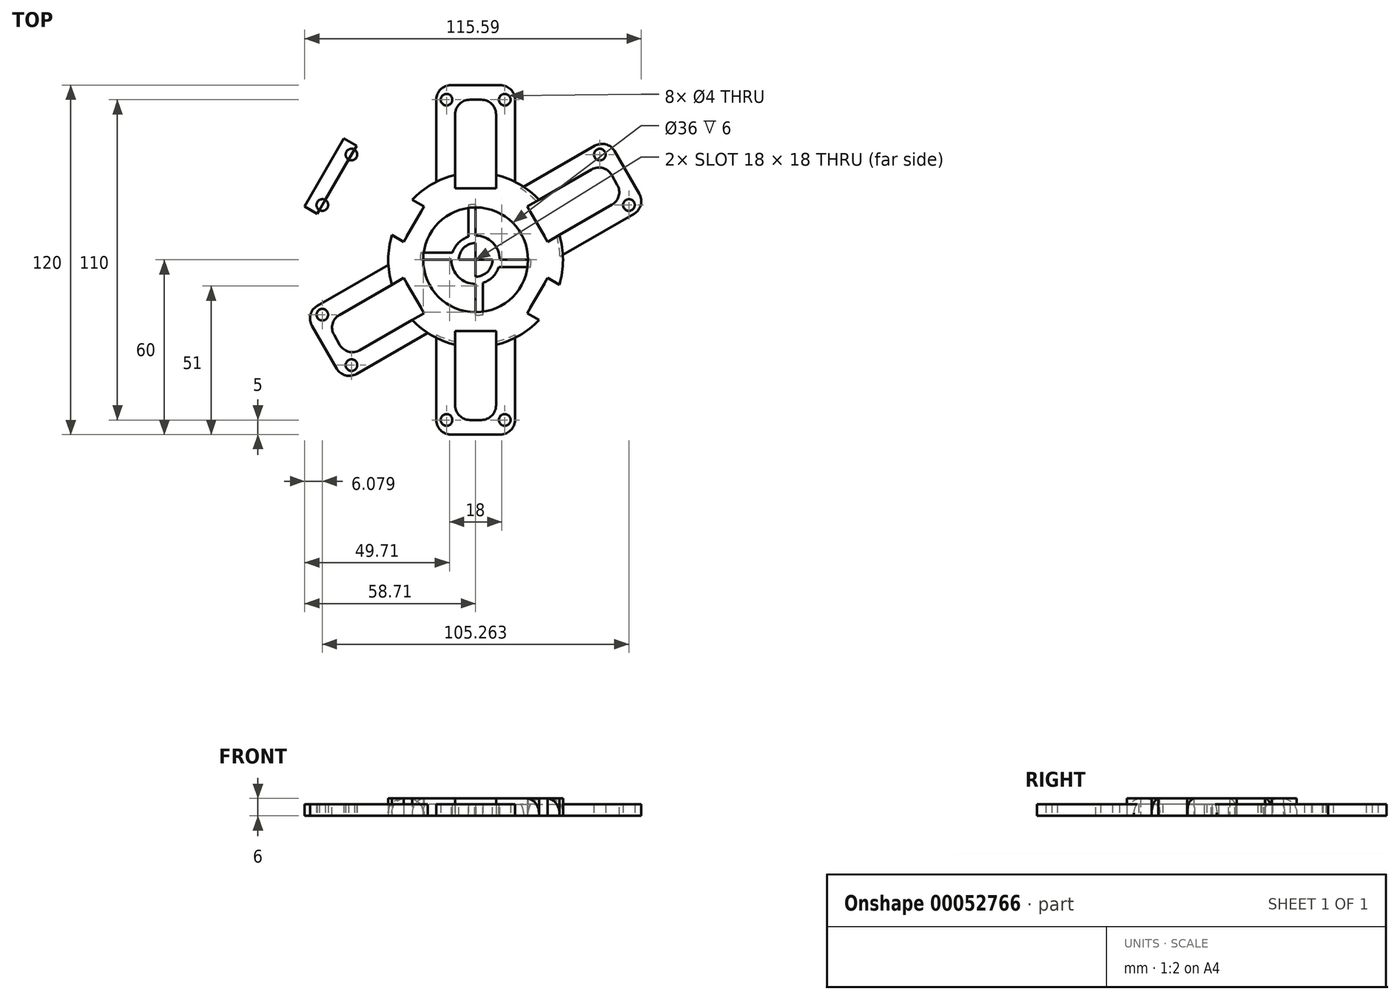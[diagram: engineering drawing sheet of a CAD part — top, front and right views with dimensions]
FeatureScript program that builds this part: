
annotation { "Feature Type Name" : "Feature", "Feature Type Description" : "" }
export const myFeature = defineFeature(function(context is Context, id is Id, definition is map)
    precondition{}
    {
        {
            assignVariable(context, id + "F0", {"name" : "RingH", "anyValue" : 6});
        }
        {
            assignVariable(context, id + "F1", {"name" : "CenterH", "anyValue" : 4});
        }
        {
            var Q0;
            Q0=qCreatedBy(makeId("Top.planeOp"),FACE);
            var sketch = newSketch(context, id + "F2", { "sketchPlane" : qUnion([Q0])});
            skCircle(sketch, "E0", {"center": v(0, 0) * mm, "radius": 18 * mm});
            skArc(sketch, "E1", {"start": v(7, -29.17) * mm, "mid": v(0, 30) * mm, "end": v(-7, -29.17) * mm});
            skLineSegment(sketch, "E2.top", {"start": v(-13.5, -60) * mm, "end": v(13.5, -60) * mm});
            skLineSegment(sketch, "E3", {"start": v(-13.5, -26.8) * mm, "end": v(-13.5, -60) * mm});
            skLineSegment(sketch, "E4", {"start": v(13.5, -26.8) * mm, "end": v(13.5, -60) * mm});
            skLineSegment(sketch, "E5.1.0", {"start": v(58.71, 18.3) * mm, "end": v(45.21, 41.7) * mm});
            skLineSegment(sketch, "E5.1.1", {"start": v(16.45, 25.09) * mm, "end": v(45.21, 41.7) * mm});
            skLineSegment(sketch, "E5.1.2", {"start": v(29.95, 1.7) * mm, "end": v(58.71, 18.3) * mm});
            skLineSegment(sketch, "E5.2.0", {"start": v(-45.21, 41.7) * mm, "end": v(-58.71, 18.3) * mm});
            skLineSegment(sketch, "E5.2.1", {"start": v(-29.95, 1.7) * mm, "end": v(-58.71, 18.3) * mm});
            skLineSegment(sketch, "E5.2.2", {"start": v(-16.45, 25.09) * mm, "end": v(-45.21, 41.7) * mm});
            skLineSegment(sketch, "E6.0", {"start": v(-40.13, 40.5) * mm, "end": v(-55.13, 14.5) * mm});
            skLineSegment(sketch, "E7.0", {"start": v(52.63, 18.84) * mm, "end": v(51.63, 20.57) * mm});
            skPoint(sketch, "E8", {"position": v(-47.63, 27.5) * mm});
            skPoint(sketch, "E9", {"position": v(-42.63, 36.16) * mm});
            skPoint(sketch, "E10", {"position": v(-52.63, 18.84) * mm});
            skCircle(sketch, "E11", {"center": v(-42.63, 36.16) * mm, "radius": 2 * mm});
            skCircle(sketch, "E12", {"center": v(-52.63, 18.84) * mm, "radius": 2 * mm});
            skPoint(sketch, "E13", {"position": v(47.63, 27.5) * mm});
            skPoint(sketch, "E14", {"position": v(42.63, 36.16) * mm});
            skPoint(sketch, "E15", {"position": v(52.63, 18.84) * mm});
            skCircle(sketch, "E16", {"center": v(42.63, 36.16) * mm, "radius": 2 * mm});
            skCircle(sketch, "E17", {"center": v(52.63, 18.84) * mm, "radius": 2 * mm});
            skPoint(sketch, "E18.orphan", {"position": v(40.13, 40.5) * mm});
            skLineSegment(sketch, "E19.trimOffspring", {"start": v(43.63, 34.43) * mm, "end": v(42.63, 36.16) * mm});
            skPoint(sketch, "E20.orphan", {"position": v(55.13, 14.5) * mm});
            skPoint(sketch, "E21", {"position": v(0, -53.3) * mm});
            skPoint(sketch, "E22", {"position": v(-10, -55) * mm});
            skPoint(sketch, "E23", {"position": v(10, -55) * mm});
            skCircle(sketch, "E24", {"center": v(10, -55) * mm, "radius": 2 * mm});
            skCircle(sketch, "E25", {"center": v(-10, -55) * mm, "radius": 2 * mm});
            skLineSegment(sketch, "E26.trimOffspring", {"start": v(8.95, -53.3) * mm, "end": v(11.05, -53.3) * mm});
            skLineSegment(sketch, "E27.trimOffspring", {"start": v(-10.56, -55) * mm, "end": v(-10, -55) * mm});
            skPoint(sketch, "E28.0.start.orphan", {"position": v(-15, -53.3) * mm});
            skPoint(sketch, "E29.orphan", {"position": v(15, -53.3) * mm});
            skLineSegment(sketch, "E30", {"start": v(0, -24.51) * mm, "end": v(0, -53.3) * mm, "construction": true});
            skLineSegment(sketch, "E31.0", {"start": v(-7, -24.51) * mm, "end": v(-7, -55) * mm});
            skLineSegment(sketch, "E32.0", {"start": v(7, -24.51) * mm, "end": v(7, -55) * mm});
            skLineSegment(sketch, "E33", {"start": v(-7, -24.51) * mm, "end": v(7, -24.51) * mm});
            skLineSegment(sketch, "E34", {"start": v(-7, -55) * mm, "end": v(7, -55) * mm});
            skLineSegment(sketch, "E35.1.0", {"start": v(17.73, 18.32) * mm, "end": v(44.13, 33.56) * mm});
            skLineSegment(sketch, "E35.1.1", {"start": v(24.73, 6.2) * mm, "end": v(51.13, 21.44) * mm});
            skLineSegment(sketch, "E35.1.2", {"start": v(51.13, 21.44) * mm, "end": v(44.13, 33.56) * mm});
            skLineSegment(sketch, "E35.1.3", {"start": v(24.73, 6.2) * mm, "end": v(17.73, 18.32) * mm});
            skLineSegment(sketch, "E35.2.0", {"start": v(-24.73, 6.2) * mm, "end": v(-51.13, 21.44) * mm});
            skLineSegment(sketch, "E35.2.1", {"start": v(-17.73, 18.32) * mm, "end": v(-44.13, 33.56) * mm});
            skLineSegment(sketch, "E35.2.2", {"start": v(-44.13, 33.56) * mm, "end": v(-51.13, 21.44) * mm});
            skLineSegment(sketch, "E35.2.3", {"start": v(-17.73, 18.32) * mm, "end": v(-24.73, 6.2) * mm});
            skLineSegment(sketch, "E36.1.0", {"start": v(17.73, -18.32) * mm, "end": v(24.73, -6.2) * mm});
            skLineSegment(sketch, "E36.1.1", {"start": v(24.73, -6.2) * mm, "end": v(51.13, -21.44) * mm});
            skLineSegment(sketch, "E36.1.2", {"start": v(17.73, -18.32) * mm, "end": v(44.13, -33.56) * mm});
            skLineSegment(sketch, "E36.3.0", {"start": v(7, 24.51) * mm, "end": v(-7, 24.51) * mm});
            skLineSegment(sketch, "E36.3.1", {"start": v(-7, 24.51) * mm, "end": v(-7, 55) * mm});
            skLineSegment(sketch, "E36.3.2", {"start": v(7, 24.51) * mm, "end": v(7, 55) * mm});
            skLineSegment(sketch, "E36.5.0", {"start": v(-24.73, -6.2) * mm, "end": v(-17.73, -18.32) * mm});
            skLineSegment(sketch, "E36.5.1", {"start": v(-17.73, -18.32) * mm, "end": v(-44.13, -33.56) * mm});
            skLineSegment(sketch, "E36.5.2", {"start": v(-24.73, -6.2) * mm, "end": v(-51.13, -21.44) * mm});
            skSolve(sketch);
        }
        {
            var Q0;
            Q0=makeQuery(id+"F2.imprint","IMPRINT",FACE,{"disambiguationData":[TD([[makeQuery(id+"F2.imprint","IMPRINT",EDGE,{"derivedFrom":sQuery(id+"F2.wireOp",EDGE,"E0")}),-1.0]])]});
            extrude(context, id + "F3", {"entities" : qUnion([Q0]), "depth" : (getVariable(context, 'RingH')) * mm});
        }
        {
            var Q0;
            Q0=makeQuery(id+"F2.imprint","IMPRINT",FACE,{"disambiguationData":[TD([[makeQuery(id+"F2.imprint","IMPRINT",EDGE,{"derivedFrom":sQuery(id+"F2.wireOp",EDGE,"E0")}),1.0]])]});
            extrude(context, id + "F4", {"entities" : qUnion([Q0]), "operationType" : NewBodyOperationType.ADD, "depth" : (getVariable(context, 'CenterH')) * mm});
        }
        {
            var Q0;
            Q0=makeQuery(id+"F2.imprint","IMPRINT",FACE,{"disambiguationData":[TD([[makeQuery(id+"F2.imprint","IMPRINT",EDGE,{"derivedFrom":sQuery(id+"F2.wireOp",EDGE,"E5.2.0")}),1.0]])]});
            var Q1;
            Q1=makeQuery(id+"F2.imprint","IMPRINT",FACE,{"disambiguationData":[TD([[makeQuery(id+"F2.imprint","IMPRINT",EDGE,{"derivedFrom":sQuery(id+"F2.wireOp",EDGE,"E2.top")}),1.0]])]});
            var Q2;
            {var subQ5=sQuery(id+"F2.wireOp",EDGE,"E7.0");Q2=makeQuery(id+"F2.imprint","IMPRINT",FACE,{"disambiguationData":[TD([[makeQuery(id+"F2.imprint","IMPRINT",EDGE,{"derivedFrom":subQ5}),1.0]])]});}
            var Q3;
            {var subQ0=sQuery(id+"F2.wireOp",EDGE,"E5.1.0");Q3=makeQuery(id+"F2.imprint","IMPRINT",FACE,{"disambiguationData":[TD([[makeQuery(id+"F2.imprint","IMPRINT",EDGE,{"derivedFrom":subQ0}),1.0]])]});}
            var Q4;
            {var subQ5=sQuery(id+"F2.wireOp",EDGE,"E28.0");Q4=makeQuery(id+"F2.imprint","IMPRINT",FACE,{"disambiguationData":[TD([[makeQuery(id+"F2.imprint","IMPRINT",EDGE,{"derivedFrom":subQ5}),1.0]])]});}
            var Q5;
            {var subQ5=sQuery(id+"F2.wireOp",EDGE,"E6.0");Q5=makeQuery(id+"F2.imprint","IMPRINT",FACE,{"disambiguationData":[TD([[makeQuery(id+"F2.imprint","IMPRINT",EDGE,{"derivedFrom":subQ5}),1.0]])]});}
            extrude(context, id + "F5", {"entities" : qUnion([Q0, Q1, Q2, Q3, Q4, Q5]), "operationType" : NewBodyOperationType.ADD, "depth" : 4 * mm});
        }
        {
            var Q0;
            Q0=qCreatedBy(makeId("Front.planeOp"),FACE);
            var sketch = newSketch(context, id + "F6", { "sketchPlane" : qUnion([Q0])});
            skLineSegment(sketch, "E37", {"start": v(0, 0) * mm, "end": v(0, 54.28) * mm, "construction": true});
            skSolve(sketch);
        }
        {
            var Q0;
            Q0=makeQuery(id+"F3.opExtrude","SWEPT_BODY",BODY,{"disambiguationData":[OSD([sQuery(id+"F2.wireOp",EDGE,"E0"),sQuery(id+"F2.wireOp",EDGE,"E1")])]});
            var Q1;
            Q1=sQuery(id+"F6.wireOp",EDGE,"E37");
            circularPattern(context, id + "F7", {"operationType" : NewBodyOperationType.ADD, "entities" : qUnion([Q0]), "axis" : qUnion([Q1]), "angle" : 180 * degree, "instanceCount" : 2});
        }
        {
            var Q0;
            Q0=makeQuery(id+"F4.opExtrude","CAP_FACE",FACE,{"disambiguationData":[OSD([sQuery(id+"F2.wireOp",EDGE,"E0")])],"isStart":false});
            var sketch = newSketch(context, id + "F8", { "sketchPlane" : qUnion([Q0])});
            skCircle(sketch, "E38.0.0", {"center": v(0, 0) * mm, "radius": 18 * mm});
            skCircle(sketch, "E39", {"center": v(0, 0) * mm, "radius": 5.78 * mm});
            skLineSegment(sketch, "E40", {"start": v(0, -5.78) * mm, "end": v(0, 5.78) * mm});
            skLineSegment(sketch, "E41", {"start": v(5.78, 0) * mm, "end": v(-5.78, 0) * mm});
            skCircle(sketch, "E42", {"center": v(0, 0) * mm, "radius": 0.26 * mm});
            skLineSegment(sketch, "E43", {"start": v(0, -5.78) * mm, "end": v(0, -18) * mm});
            skLineSegment(sketch, "E44", {"start": v(-5.78, 0) * mm, "end": v(-18, 0) * mm});
            skCircle(sketch, "E45", {"center": v(0, 0) * mm, "radius": 8.3 * mm});
            skLineSegment(sketch, "E46", {"start": v(0, 8.3) * mm, "end": v(0, 18) * mm});
            skLineSegment(sketch, "E47", {"start": v(8.3, 0) * mm, "end": v(18, 0) * mm});
            skLineSegment(sketch, "E48.0", {"start": v(-2.5, 8.3) * mm, "end": v(-2.5, 18) * mm});
            skLineSegment(sketch, "E49.0", {"start": v(-5.78, 2.5) * mm, "end": v(-18, 2.5) * mm});
            skLineSegment(sketch, "E50.0", {"start": v(2.5, -5.78) * mm, "end": v(2.5, -18) * mm});
            skLineSegment(sketch, "E51.0", {"start": v(8.3, -2.5) * mm, "end": v(18, -2.5) * mm});
            skLineSegment(sketch, "E52", {"start": v(8.3, -2.5) * mm, "end": v(7.53, -2.5) * mm});
            skLineSegment(sketch, "E53", {"start": v(-2.5, 8.3) * mm, "end": v(-2.5, 6.46) * mm});
            skSolve(sketch);
        }
        {
            var Q0;
            {var subQ0=sQuery(id+"F8.wireOp",EDGE,"E40");var subQ1=sQuery(id+"F8.wireOp",EDGE,"E39");var subQ2=makeQuery(id+"F8.imprint","INTERSECT",VERTEX,{"disambiguationData":[OD(0.0)],"derivedFrom":[subQ1,subQ0]});Q0=makeQuery(id+"F8.imprint","IMPRINT",FACE,{"disambiguationData":[TD([[makeQuery(id+"F8.imprint","IMPRINT",EDGE,{"disambiguationData":[TD([[subQ2,-1.0]])],"derivedFrom":subQ1}),1.0]])]});}
            var Q1;
            {var subQ0=sQuery(id+"F8.wireOp",EDGE,"E40");var subQ1=sQuery(id+"F8.wireOp",EDGE,"E39");var subQ2=makeQuery(id+"F8.imprint","INTERSECT",VERTEX,{"disambiguationData":[OD(1.0)],"derivedFrom":[subQ1,subQ0]});Q1=makeQuery(id+"F8.imprint","IMPRINT",FACE,{"disambiguationData":[TD([[makeQuery(id+"F8.imprint","IMPRINT",EDGE,{"disambiguationData":[TD([[subQ2,-1.0]])],"derivedFrom":subQ1}),1.0]])]});}
            var Q2;
            {var subQ1=sQuery(id+"F8.wireOp",EDGE,"E39");var subQ3=sQuery(id+"F8.wireOp",EDGE,"E41");var subQ4=makeQuery(id+"F8.imprint","INTERSECT",VERTEX,{"derivedFrom":[subQ1,subQ3]});Q2=makeQuery(id+"F8.imprint","IMPRINT",FACE,{"disambiguationData":[TD([[makeQuery(id+"F8.imprint","IMPRINT",EDGE,{"disambiguationData":[TD([[subQ4,-1.0]])],"derivedFrom":subQ3}),1.0]])]});}
            var Q3;
            {var subQ0=sQuery(id+"F8.wireOp",EDGE,"E46");Q3=makeQuery(id+"F8.imprint","IMPRINT",FACE,{"disambiguationData":[TD([[makeQuery(id+"F8.imprint","IMPRINT",EDGE,{"derivedFrom":subQ0}),-1.0]])]});}
            var Q4;
            {var subQ0=sQuery(id+"F8.wireOp",EDGE,"E43");var subQ1=sQuery(id+"F8.wireOp",EDGE,"E38.0.0");var subQ2=makeQuery(id+"F8.imprint","INTERSECT",VERTEX,{"derivedFrom":[subQ1,subQ0]});Q4=makeQuery(id+"F8.imprint","IMPRINT",FACE,{"disambiguationData":[TD([[makeQuery(id+"F8.imprint","IMPRINT",EDGE,{"disambiguationData":[TD([[subQ2,1.0]])],"derivedFrom":subQ1}),1.0]])]});}
            var Q5;
            {var subQ1=sQuery(id+"F8.wireOp",EDGE,"E38.0.0");var subQ6=sQuery(id+"F8.wireOp",EDGE,"E48.0");var subQ8=makeQuery(id+"F8.imprint","INTERSECT",VERTEX,{"derivedFrom":[subQ1,subQ6]});Q5=makeQuery(id+"F8.imprint","IMPRINT",FACE,{"disambiguationData":[TD([[makeQuery(id+"F8.imprint","IMPRINT",EDGE,{"disambiguationData":[TD([[subQ8,-1.0]])],"derivedFrom":subQ1}),1.0]])]});}
            var Q6;
            {var subQ3=sQuery(id+"F8.wireOp",EDGE,"E38.0.0");var subQ7=sQuery(id+"F8.wireOp",EDGE,"E50.0");var subQ8=makeQuery(id+"F8.imprint","INTERSECT",VERTEX,{"derivedFrom":[subQ3,subQ7]});Q6=makeQuery(id+"F8.imprint","IMPRINT",FACE,{"disambiguationData":[TD([[makeQuery(id+"F8.imprint","IMPRINT",EDGE,{"disambiguationData":[TD([[subQ8,-1.0]])],"derivedFrom":subQ3}),1.0]])]});}
            extrude(context, id + "F9", {"entities" : qUnion([Q0, Q1, Q2, Q3, Q4, Q5, Q6]), "operationType" : NewBodyOperationType.REMOVE, "oppositeDirection" : true, "depth" : 25 * mm});
        }
        {
            var Q0;
            Q0=makeQuery(id+"F7.opPattern","COPY",EDGE,{"derivedFrom":makeQuery(id+"F5.opExtrude","SWEPT_EDGE",EDGE,{"disambiguationData":[OSD([sQuery(id+"F2.wireOp",EDGE,"E5.1.0"),sQuery(id+"F2.wireOp",EDGE,"E5.1.1")])]}),"instanceName":"1"});
            var Q1;
            Q1=makeQuery(id+"F5.opExtrude","SWEPT_EDGE",EDGE,{"disambiguationData":[OSD([sQuery(id+"F2.wireOp",EDGE,"E2.top"),sQuery(id+"F2.wireOp",EDGE,"E3")])]});
            var Q2;
            Q2=makeQuery(id+"F5.opExtrude","SWEPT_EDGE",EDGE,{"disambiguationData":[OSD([sQuery(id+"F2.wireOp",EDGE,"E2.top"),sQuery(id+"F2.wireOp",EDGE,"E4")])]});
            var Q3;
            Q3=makeQuery(id+"F7.opPattern","COPY",EDGE,{"derivedFrom":makeQuery(id+"F5.opExtrude","SWEPT_EDGE",EDGE,{"disambiguationData":[OSD([sQuery(id+"F2.wireOp",EDGE,"E5.2.0"),sQuery(id+"F2.wireOp",EDGE,"E5.2.2")])]}),"instanceName":"1"});
            var Q4;
            {var subQ0=sQuery(id+"F2.wireOp",EDGE,"E1");var subQ1=makeQuery(id+"F2.imprint","INTERSECT",VERTEX,{"derivedFrom":[subQ0,sQuery(id+"F2.wireOp",EDGE,"E4")]});Q4=makeQuery(id+"F3.opExtrude","CAP_EDGE",EDGE,{"disambiguationData":[OSD([subQ0]),TDD([makeQuery(id+"F2.imprint","IMPRINT",EDGE,{"disambiguationData":[TD([[makeQuery(id+"F2.imprint","INTERSECT",VERTEX,{"derivedFrom":[subQ0,sQuery(id+"F2.wireOp",EDGE,"E32.0")]}),-1.0]])],"derivedFrom":subQ0}),makeQuery(id+"F2.imprint","IMPRINT",EDGE,{"disambiguationData":[TD([[subQ1,-1.0]])],"derivedFrom":subQ0})])],"isStart":false});}
            var Q5;
            Q5=makeQuery(id+"F7.opPattern","COPY",EDGE,{"derivedFrom":makeQuery(id+"F5.opExtrude","SWEPT_EDGE",EDGE,{"disambiguationData":[OSD([sQuery(id+"F2.wireOp",EDGE,"E5.2.0"),sQuery(id+"F2.wireOp",EDGE,"E5.2.1")])]}),"instanceName":"1"});
            var Q6;
            {var subQ0=sQuery(id+"F2.wireOp",EDGE,"E1");var subQ1=makeQuery(id+"F2.imprint","INTERSECT",VERTEX,{"derivedFrom":[subQ0,sQuery(id+"F2.wireOp",EDGE,"E3")]});Q6=makeQuery(id+"F3.opExtrude","CAP_EDGE",EDGE,{"disambiguationData":[OSD([subQ0]),TDD([makeQuery(id+"F2.imprint","IMPRINT",EDGE,{"disambiguationData":[TD([[subQ1,1.0]])],"derivedFrom":subQ0}),makeQuery(id+"F2.imprint","IMPRINT",EDGE,{"disambiguationData":[TD([[makeQuery(id+"F2.imprint","INTERSECT",VERTEX,{"derivedFrom":[subQ0,sQuery(id+"F2.wireOp",EDGE,"E31.0")]}),1.0]])],"derivedFrom":subQ0})])],"isStart":false});}
            var Q7;
            Q7=makeQuery(id+"F7.opPattern","COPY",EDGE,{"derivedFrom":makeQuery(id+"F5.opExtrude","SWEPT_EDGE",EDGE,{"disambiguationData":[OSD([sQuery(id+"F2.wireOp",EDGE,"E5.1.0"),sQuery(id+"F2.wireOp",EDGE,"E5.1.2")])]}),"instanceName":"1"});
            var Q8;
            {var subQ0=sQuery(id+"F2.wireOp",EDGE,"E1");var subQ1=makeQuery(id+"F2.imprint","INTERSECT",VERTEX,{"derivedFrom":[subQ0,sQuery(id+"F2.wireOp",EDGE,"E5.2.1")]});Q8=makeQuery(id+"F3.opExtrude","CAP_EDGE",EDGE,{"disambiguationData":[OSD([subQ0]),TDD([makeQuery(id+"F2.imprint","IMPRINT",EDGE,{"disambiguationData":[TD([[subQ1,1.0]])],"derivedFrom":subQ0}),makeQuery(id+"F2.imprint","IMPRINT",EDGE,{"disambiguationData":[TD([[subQ1,-1.0]])],"derivedFrom":subQ0})])],"isStart":false});}
            var Q9;
            Q9=makeQuery(id+"F3.opExtrude","CAP_EDGE",EDGE,{"disambiguationData":[OSD([sQuery(id+"F2.wireOp",EDGE,"E0")])],"isStart":false});
            var Q10;
            Q10=makeQuery(id+"F5.opExtrude","SWEPT_EDGE",EDGE,{"disambiguationData":[OSD([sQuery(id+"F2.wireOp",EDGE,"E5.2.0"),sQuery(id+"F2.wireOp",EDGE,"E5.2.1")])]});
            var Q11;
            Q11=makeQuery(id+"F5.opExtrude","SWEPT_EDGE",EDGE,{"disambiguationData":[OSD([sQuery(id+"F2.wireOp",EDGE,"E5.2.0"),sQuery(id+"F2.wireOp",EDGE,"E5.2.2")])]});
            var Q12;
            {var subQ0=sQuery(id+"F2.wireOp",EDGE,"E1");var subQ1=makeQuery(id+"F2.imprint","INTERSECT",VERTEX,{"derivedFrom":[subQ0,sQuery(id+"F2.wireOp",EDGE,"E5.2.2")]});Q12=makeQuery(id+"F3.opExtrude","CAP_EDGE",EDGE,{"disambiguationData":[OSD([subQ0]),TDD([makeQuery(id+"F2.imprint","IMPRINT",EDGE,{"disambiguationData":[TD([[subQ1,1.0]])],"derivedFrom":subQ0}),makeQuery(id+"F2.imprint","IMPRINT",EDGE,{"disambiguationData":[TD([[subQ1,-1.0]])],"derivedFrom":subQ0})])],"isStart":false});}
            var Q13;
            {var subQ0=sQuery(id+"F2.wireOp",EDGE,"E1");var subQ1=makeQuery(id+"F2.imprint","INTERSECT",VERTEX,{"derivedFrom":[subQ0,sQuery(id+"F2.wireOp",EDGE,"E5.1.1")]});Q13=makeQuery(id+"F3.opExtrude","CAP_EDGE",EDGE,{"disambiguationData":[OSD([subQ0]),TDD([makeQuery(id+"F2.imprint","IMPRINT",EDGE,{"disambiguationData":[TD([[subQ1,1.0]])],"derivedFrom":subQ0}),makeQuery(id+"F2.imprint","IMPRINT",EDGE,{"disambiguationData":[TD([[subQ1,-1.0]])],"derivedFrom":subQ0})])],"isStart":false});}
            var Q14;
            Q14=makeQuery(id+"F7.opPattern","COPY",EDGE,{"derivedFrom":makeQuery(id+"F5.opExtrude","SWEPT_EDGE",EDGE,{"disambiguationData":[OSD([sQuery(id+"F2.wireOp",EDGE,"E2.top"),sQuery(id+"F2.wireOp",EDGE,"E4")])]}),"instanceName":"1"});
            var Q15;
            Q15=makeQuery(id+"F7.opPattern","COPY",EDGE,{"derivedFrom":makeQuery(id+"F5.opExtrude","SWEPT_EDGE",EDGE,{"disambiguationData":[OSD([sQuery(id+"F2.wireOp",EDGE,"E2.top"),sQuery(id+"F2.wireOp",EDGE,"E3")])]}),"instanceName":"1"});
            var Q16;
            Q16=makeQuery(id+"F5.opExtrude","SWEPT_EDGE",EDGE,{"disambiguationData":[OSD([sQuery(id+"F2.wireOp",EDGE,"E5.1.0"),sQuery(id+"F2.wireOp",EDGE,"E5.1.1")])]});
            var Q17;
            Q17=makeQuery(id+"F5.opExtrude","SWEPT_EDGE",EDGE,{"disambiguationData":[OSD([sQuery(id+"F2.wireOp",EDGE,"E5.1.0"),sQuery(id+"F2.wireOp",EDGE,"E5.1.2")])]});
            var Q18;
            {var subQ0=sQuery(id+"F2.wireOp",EDGE,"E1");var subQ1=makeQuery(id+"F2.imprint","INTERSECT",VERTEX,{"derivedFrom":[subQ0,sQuery(id+"F2.wireOp",EDGE,"E5.1.2")]});Q18=makeQuery(id+"F3.opExtrude","CAP_EDGE",EDGE,{"disambiguationData":[OSD([subQ0]),TDD([makeQuery(id+"F2.imprint","IMPRINT",EDGE,{"disambiguationData":[TD([[subQ1,1.0]])],"derivedFrom":subQ0}),makeQuery(id+"F2.imprint","IMPRINT",EDGE,{"disambiguationData":[TD([[subQ1,-1.0]])],"derivedFrom":subQ0})])],"isStart":false});}
            var Q19;
            Q19=makeQuery(id+"F7.opPattern","COPY",EDGE,{"derivedFrom":makeQuery(id+"F5.opExtrude","SWEPT_EDGE",EDGE,{"disambiguationData":[OSD([sQuery(id+"F2.wireOp",EDGE,"E6.0"),sQuery(id+"F2.wireOp",EDGE,"E35.2.2"),sQuery(id+"F2.wireOp",EDGE,"E35.2.0")])]}),"instanceName":"1"});
            var Q20;
            Q20=makeQuery(id+"F5.opExtrude","SWEPT_EDGE",EDGE,{"disambiguationData":[OSD([sQuery(id+"F2.wireOp",EDGE,"E35.1.2"),sQuery(id+"F2.wireOp",EDGE,"E35.1.1")])]});
            var Q21;
            Q21=makeQuery(id+"F5.opExtrude","SWEPT_EDGE",EDGE,{"disambiguationData":[OSD([sQuery(id+"F2.wireOp",EDGE,"E35.1.2"),sQuery(id+"F2.wireOp",EDGE,"E35.1.0")])]});
            var Q22;
            Q22=makeQuery(id+"F5.opExtrude","SWEPT_EDGE",EDGE,{"disambiguationData":[OSD([sQuery(id+"F2.wireOp",EDGE,"E6.0"),sQuery(id+"F2.wireOp",EDGE,"E35.2.2"),sQuery(id+"F2.wireOp",EDGE,"E35.2.1")])]});
            var Q23;
            Q23=makeQuery(id+"F5.opExtrude","SWEPT_EDGE",EDGE,{"disambiguationData":[OSD([sQuery(id+"F2.wireOp",EDGE,"E6.0"),sQuery(id+"F2.wireOp",EDGE,"E35.2.2"),sQuery(id+"F2.wireOp",EDGE,"E35.2.0")])]});
            var Q24;
            Q24=makeQuery(id+"F7.opPattern","COPY",EDGE,{"derivedFrom":makeQuery(id+"F5.opExtrude","SWEPT_EDGE",EDGE,{"disambiguationData":[OSD([sQuery(id+"F2.wireOp",EDGE,"E32.0"),sQuery(id+"F2.wireOp",EDGE,"E34")])]}),"instanceName":"1"});
            var Q25;
            Q25=makeQuery(id+"F7.opPattern","COPY",EDGE,{"derivedFrom":makeQuery(id+"F5.opExtrude","SWEPT_EDGE",EDGE,{"disambiguationData":[OSD([sQuery(id+"F2.wireOp",EDGE,"E35.1.2"),sQuery(id+"F2.wireOp",EDGE,"E35.1.1")])]}),"instanceName":"1"});
            var Q26;
            Q26=makeQuery(id+"F7.opPattern","COPY",EDGE,{"derivedFrom":makeQuery(id+"F5.opExtrude","SWEPT_EDGE",EDGE,{"disambiguationData":[OSD([sQuery(id+"F2.wireOp",EDGE,"E6.0"),sQuery(id+"F2.wireOp",EDGE,"E35.2.2"),sQuery(id+"F2.wireOp",EDGE,"E35.2.1")])]}),"instanceName":"1"});
            var Q27;
            Q27=makeQuery(id+"F5.opExtrude","SWEPT_EDGE",EDGE,{"disambiguationData":[OSD([sQuery(id+"F2.wireOp",EDGE,"E31.0"),sQuery(id+"F2.wireOp",EDGE,"E34")])]});
            var Q28;
            Q28=makeQuery(id+"F5.opExtrude","SWEPT_EDGE",EDGE,{"disambiguationData":[OSD([sQuery(id+"F2.wireOp",EDGE,"E32.0"),sQuery(id+"F2.wireOp",EDGE,"E34")])]});
            var Q29;
            Q29=makeQuery(id+"F7.opPattern","COPY",EDGE,{"derivedFrom":makeQuery(id+"F5.opExtrude","SWEPT_EDGE",EDGE,{"disambiguationData":[OSD([sQuery(id+"F2.wireOp",EDGE,"E35.1.2"),sQuery(id+"F2.wireOp",EDGE,"E35.1.0")])]}),"instanceName":"1"});
            var Q30;
            Q30=makeQuery(id+"F7.opPattern","COPY",EDGE,{"derivedFrom":makeQuery(id+"F5.opExtrude","SWEPT_EDGE",EDGE,{"disambiguationData":[OSD([sQuery(id+"F2.wireOp",EDGE,"E31.0"),sQuery(id+"F2.wireOp",EDGE,"E34")])]}),"instanceName":"1"});
            fillet(context, id + "F10", {"entities" : qUnion([Q0, Q1, Q2, Q3, Q4, Q5, Q6, Q7, Q8, Q9, Q10, Q11, Q12, Q13, Q14, Q15, Q16, Q17, Q18, Q19, Q20, Q21, Q22, Q23, Q24, Q25, Q26, Q27, Q28, Q29, Q30]), "radius" : 5 * mm, "tangentPropagation" : true, "allowEdgeOverflow" : false});
        }
    });
